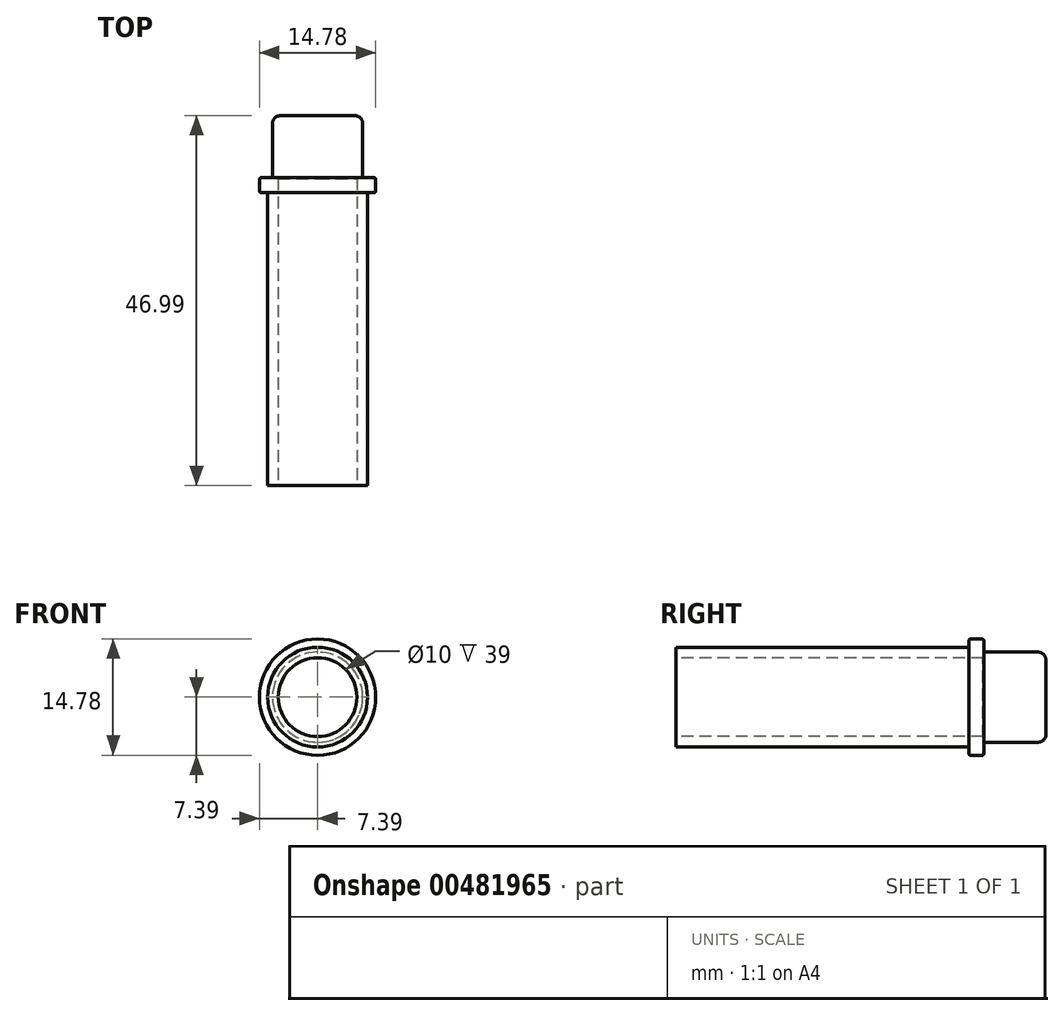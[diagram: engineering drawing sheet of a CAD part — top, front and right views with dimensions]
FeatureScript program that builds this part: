
annotation { "Feature Type Name" : "Feature", "Feature Type Description" : "" }
export const myFeature = defineFeature(function(context is Context, id is Id, definition is map)
    precondition{}
    {
        {
            var Q0;
            Q0=qCreatedBy(makeId("Top.planeOp"),FACE);
            var sketch = newSketch(context, id + "F0", { "sketchPlane" : qUnion([Q0])});
            skLineSegment(sketch, "E0", {"start": v(0, -37.18) * mm, "end": v(0, 10.53) * mm});
            skPoint(sketch, "E1.start.orphan", {"position": v(-7.39, 0) * mm});
            skLineSegment(sketch, "E2", {"start": v(0, -37.18) * mm, "end": v(-6.34, -37.18) * mm});
            skLineSegment(sketch, "E3", {"start": v(-6.34, -37.18) * mm, "end": v(-6.34, 0) * mm});
            skLineSegment(sketch, "E4", {"start": v(-6.34, 0) * mm, "end": v(-7.39, 0) * mm});
            skLineSegment(sketch, "E5", {"start": v(-7.39, 1.94) * mm, "end": v(-7.39, 0) * mm});
            skLineSegment(sketch, "E6", {"start": v(-7.39, 1.94) * mm, "end": v(-5.73, 1.94) * mm});
            skLineSegment(sketch, "E7", {"start": v(-5.73, 1.94) * mm, "end": v(-5.73, 9.8) * mm});
            skLineSegment(sketch, "E8", {"start": v(-5.73, 9.8) * mm, "end": v(0, 9.81) * mm});
            skSolve(sketch);
        }
        {
            var Q0;
            Q0 = qSketchRegion(id + "F0", true);
            var Q1;
            Q1=sQuery(id+"F0.wireOp",EDGE,"E0");
            revolve(context, id + "F1", {"entities" : qUnion([Q0]), "axis" : qUnion([Q1]), "revolveType" : RevolveType.FULL});
        }
        {
            var Q0;
            Q0=makeQuery(id+"F1.opRevolve","SWEPT_EDGE",EDGE,{"disambiguationData":[OSD([sQuery(id+"F0.wireOp",EDGE,"E7"),sQuery(id+"F0.wireOp",EDGE,"E8")])]});
            fillet(context, id + "F2", {"entities" : qUnion([Q0]), "radius" : 1 * mm, "tangentPropagation" : true, "allowEdgeOverflow" : false});
        }
        {
            var Q0;
            Q0=makeQuery(id+"F1.opRevolve","SWEPT_EDGE",EDGE,{"disambiguationData":[OSD([sQuery(id+"F0.wireOp",EDGE,"E5"),sQuery(id+"F0.wireOp",EDGE,"E6")])]});
            var Q1;
            Q1=makeQuery(id+"F1.opRevolve","SWEPT_FACE",FACE,{"disambiguationData":[OSD([sQuery(id+"F0.wireOp",EDGE,"E5")])]});
            fillet(context, id + "F3", {"entities" : qUnion([Q0, Q1]), "radius" : .25 * mm, "tangentPropagation" : true, "allowEdgeOverflow" : false});
        }
        {
            var Q0;
            Q0=makeQuery(id+"F1.opRevolve","SWEPT_FACE",FACE,{"disambiguationData":[OSD([sQuery(id+"F0.wireOp",EDGE,"E2")])]});
            var sketch = newSketch(context, id + "F4", { "sketchPlane" : qUnion([Q0])});
            skCircle(sketch, "E9", {"center": v(0, 0) * mm, "radius": 5 * mm});
            skSolve(sketch);
        }
        {
            var Q0;
            Q0 = qSketchRegion(id + "F4", true);
            extrude(context, id + "F5", {"entities" : qUnion([Q0]), "operationType" : NewBodyOperationType.REMOVE, "oppositeDirection" : true, "depth" : 39 * mm});
        }
    });
